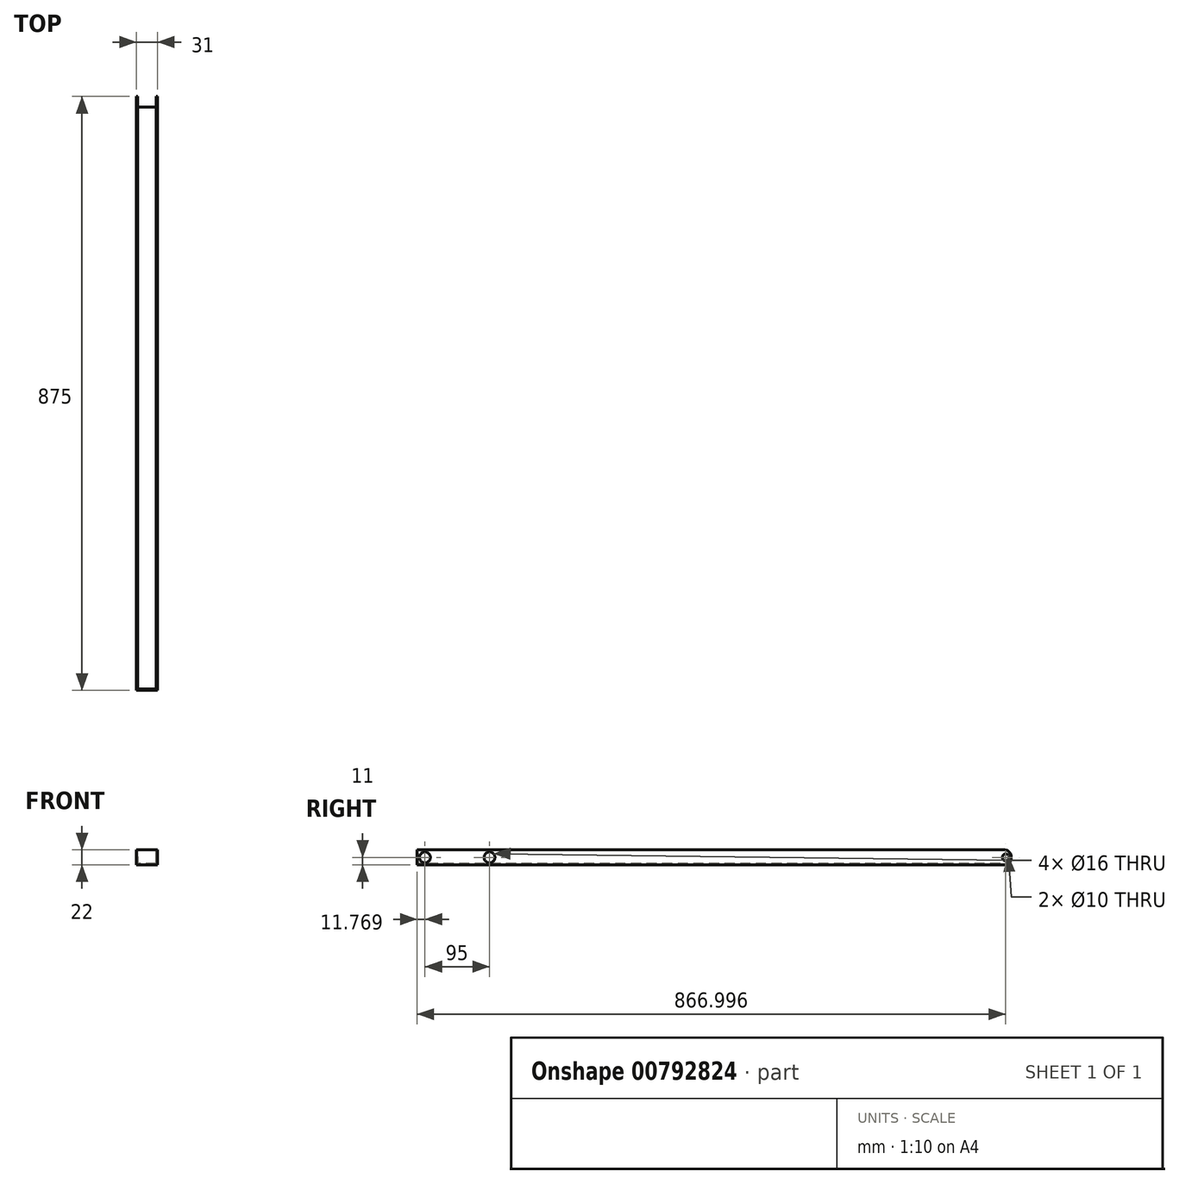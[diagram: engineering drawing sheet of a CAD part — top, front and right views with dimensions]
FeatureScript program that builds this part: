
annotation { "Feature Type Name" : "Feature", "Feature Type Description" : "" }
export const myFeature = defineFeature(function(context is Context, id is Id, definition is map)
    precondition{}
    {
        {
            var Q0;
            Q0=qCreatedBy(makeId("Right.planeOp"),FACE);
            var sketch = newSketch(context, id + "F0", { "sketchPlane" : qUnion([Q0])});
            skLineSegment(sketch, "E0", {"start": v(-388.26, 0) * mm, "end": v(486.74, 0) * mm});
            skLineSegment(sketch, "E1", {"start": v(486.74, 0) * mm, "end": v(486.74, -22) * mm});
            skLineSegment(sketch, "E2", {"start": v(486.74, -22) * mm, "end": v(-388.26, -22) * mm});
            skLineSegment(sketch, "E3", {"start": v(-388.26, -22) * mm, "end": v(-388.26, 0) * mm});
            skSolve(sketch);
        }
        {
            var Q0;
            Q0 = qSketchRegion(id + "F0", true);
            extrude(context, id + "F1", {"entities" : qUnion([Q0]), "oppositeDirection" : true, "depth" : 31 * mm, "offsetDistance" : 25 * mm});
        }
        {
            var Q0;
            Q0=makeQuery(id+"FNcDkWdHLqWzwqB_1.boolean.opBoolean","MERGE",FACE,{"derivedFrom":[makeQuery(id+"F1.opExtrude","SWEPT_FACE",FACE,{"disambiguationData":[OSD([sQuery(id+"F0.wireOp",EDGE,"E0")])]})],"fromTools":[makeQuery(id+"FNcDkWdHLqWzwqB_1.opExtrude","SWEPT_FACE",FACE,{"disambiguationData":[OSD([sQuery(id+"FCv60qlW79Pk3i8_1.wireOp",EDGE,"PrjJIeI4-ssgj-zgrI-7YpJ-pXO2Z5tQKrwP")])]})]});
            shell(context, id + "F2", {"entities" : qUnion([Q0]), "thickness" : 2 * mm});
        }
        {
            var Q0;
            Q0=makeQuery(id+"FVv2z1C1KTUzVl1_1.boolean.opBoolean","MERGE",FACE,{"derivedFrom":[makeQuery(id+"Fk6BJtRvKEo7X09_1.boolean.opBoolean","MERGE",FACE,{"derivedFrom":[makeQuery(id+"FNRSXFX3qVIVStC_1.boolean.opBoolean","MERGE",FACE,{"derivedFrom":[makeQuery(id+"F1.opExtrude","CAP_FACE",FACE,{"disambiguationData":[OSD([sQuery(id+"F0.wireOp",EDGE,"E0"),sQuery(id+"F0.wireOp",EDGE,"E1"),sQuery(id+"F0.wireOp",EDGE,"E2"),sQuery(id+"F0.wireOp",EDGE,"E3")])],"isStart":true}),makeQuery(id+"FNRSXFX3qVIVStC_1.opExtrude","CAP_FACE",FACE,{"disambiguationData":[OSD([sQuery(id+"FfsytLRgZImSpx3_1.wireOp",EDGE,"guVfW4hg-HYbG-UQzY-qkXY-AgcHQorrtYFj"),sQuery(id+"FfsytLRgZImSpx3_1.wireOp",EDGE,"ZCWRIXnY-XKVi-ryX6-uVYM-eQVDyBlf6B18"),sQuery(id+"FfsytLRgZImSpx3_1.wireOp",EDGE,"6apUsIMl-hWBS-8y3H-jMW6-ltsoOyLJVNbS"),sQuery(id+"FfsytLRgZImSpx3_1.wireOp",EDGE,"gpbRxTAZ-53LZ-ltw9-oope-mzS1HqgQM46F")])],"isStart":true})]}),makeQuery(id+"Fk6BJtRvKEo7X09_1.opExtrude","CAP_FACE",FACE,{"disambiguationData":[OSD([sQuery(id+"FWP3wo2K1PFairP_1.wireOp",EDGE,"RLKPXvGZ-6aeY-MFqp-uEFB-Y11XugVjV6vi"),sQuery(id+"FWP3wo2K1PFairP_1.wireOp",EDGE,"VqrrFjfu-vJZB-tzm9-Pqj7-21AsSRerqMTq"),sQuery(id+"FWP3wo2K1PFairP_1.wireOp",EDGE,"DV30RlPB-yelA-3BQe-yuDF-ZBDe1DssQMZR"),sQuery(id+"FWP3wo2K1PFairP_1.wireOp",EDGE,"hxL0ufJe-5V7Y-YkYO-v3yC-vdh2zJHQ3dM3")])],"isStart":true}),makeQuery(id+"Fk6BJtRvKEo7X09_1.opExtrude","CAP_FACE",FACE,{"disambiguationData":[OSD([sQuery(id+"FWP3wo2K1PFairP_1.wireOp",EDGE,"Iu78I8UH-Ag6m-vXnt-yIfC-VsHkMFwcecgq"),sQuery(id+"FWP3wo2K1PFairP_1.wireOp",EDGE,"J01mLQBO-0brp-1190-Uz3d-mbk1WVKgwclC"),sQuery(id+"FWP3wo2K1PFairP_1.wireOp",EDGE,"DArKGSrG-gMns-weNL-KKOz-bLA2HFYaYrMG"),sQuery(id+"FWP3wo2K1PFairP_1.wireOp",EDGE,"wbFtDD6o-eEzf-rPkh-OMWt-3cl9sizvQHqt")])],"isStart":true})]}),makeQuery(id+"FVv2z1C1KTUzVl1_1.opExtrude","CAP_FACE",FACE,{"disambiguationData":[OSD([sQuery(id+"FNLiDQGDlaEW116_1.wireOp",EDGE,"FMQFbGrz-yUS7-YStC-X8hH-naCITp3HSpcB"),sQuery(id+"FNLiDQGDlaEW116_1.wireOp",EDGE,"1a20oQKK-PTd7-pF8n-adkK-x5VS4rqthSRl"),sQuery(id+"FNLiDQGDlaEW116_1.wireOp",EDGE,"lPfx92Xd-sMOD-QXDu-w2bj-9ym4LUR5MAjY"),sQuery(id+"FNLiDQGDlaEW116_1.wireOp",EDGE,"eTXjAAXH-MWSY-cq12-PB3M-X8OxoKmDEWyC")])],"isStart":true}),makeQuery(id+"FVv2z1C1KTUzVl1_1.opExtrude","CAP_FACE",FACE,{"disambiguationData":[OSD([sQuery(id+"FNLiDQGDlaEW116_1.wireOp",EDGE,"V9W5izrU-Q6Zo-HlYU-XUtX-LOkD6KGmEAuB"),sQuery(id+"FNLiDQGDlaEW116_1.wireOp",EDGE,"562pbG6D-TJI1-XGno-75is-4YSaHXAUytCh"),sQuery(id+"FNLiDQGDlaEW116_1.wireOp",EDGE,"Zdfx7gO0-Y7jM-oHTw-9pvJ-OO3yxUAsWjtI"),sQuery(id+"FNLiDQGDlaEW116_1.wireOp",EDGE,"jmWXe39T-hYD2-V8mF-EcTK-DER7JQwctyas")])],"isStart":true}),makeQuery(id+"FVv2z1C1KTUzVl1_1.opExtrude","CAP_FACE",FACE,{"disambiguationData":[OSD([sQuery(id+"FNLiDQGDlaEW116_1.wireOp",EDGE,"KDKhPe1G-76aM-vKvb-EfsU-BXRDVSjyG5kg"),sQuery(id+"FNLiDQGDlaEW116_1.wireOp",EDGE,"2lfoMrka-jovZ-Rabm-Q0hQ-cbGMkZFnikdY"),sQuery(id+"FNLiDQGDlaEW116_1.wireOp",EDGE,"u8MqUk8a-5dgu-EIkQ-NQxV-EvjM6ESLjCmz"),sQuery(id+"FNLiDQGDlaEW116_1.wireOp",EDGE,"Ddv1R5dZ-CSrU-PeJ0-kcI9-YiED82pPoSU3")])],"isStart":true})]});
            var sketch = newSketch(context, id + "F3", { "sketchPlane" : qUnion([Q0])});
            skLineSegment(sketch, "E4", {"start": v(486.74, -11) * mm, "end": v(447.34, -11) * mm, "construction": true});
            skLineSegment(sketch, "E5", {"start": v(486.74, 12.78) * mm, "end": v(486.74, -40) * mm, "construction": true});
            skCircle(sketch, "E6", {"center": v(478.74, -11) * mm, "radius": 5 * mm});
            skSolve(sketch);
        }
        {
            var Q0;
            Q0 = qSketchRegion(id + "F3", true);
            extrude(context, id + "F4", {"entities" : qUnion([Q0]), "operationType" : NewBodyOperationType.REMOVE, "oppositeDirection" : true, "depth" : 61 * mm, "offsetDistance" : 25 * mm});
        }
        {
            var Q0;
            {var subQ7=sQuery(id+"F0.wireOp",EDGE,"E1");var subQ8=sQuery(id+"F0.wireOp",EDGE,"E0");var subQ14=makeQuery(id+"F1.opExtrude","SWEPT_FACE",FACE,{"disambiguationData":[OSD([subQ7])]});Q0=makeQuery(id+"Fk6BJtRvKEo7X09_1.boolean.opBoolean","SPLIT",FACE,{"disambiguationData":[TD([subQ14])],"derivedFrom":makeQuery(id+"FNRSXFX3qVIVStC_1.boolean.opBoolean","SPLIT",FACE,{"disambiguationData":[TD([subQ14])],"derivedFrom":makeQuery(id+"F1.opExtrude","SWEPT_FACE",FACE,{"disambiguationData":[OSD([subQ8])]})})});}
            var sketch = newSketch(context, id + "F5", { "sketchPlane" : qUnion([Q0])});
            skLineSegment(sketch, "E7.bottom", {"start": v(-10, 486.74) * mm, "end": v(-26, 486.74) * mm});
            skLineSegment(sketch, "E7.top", {"start": v(-10, 470.74) * mm, "end": v(-26, 470.74) * mm});
            skLineSegment(sketch, "E7.left", {"start": v(-10, 486.74) * mm, "end": v(-10, 470.74) * mm});
            skLineSegment(sketch, "E7.right", {"start": v(-26, 486.74) * mm, "end": v(-26, 470.74) * mm});
            skSolve(sketch);
        }
        {
            var Q0;
            Q0 = qSketchRegion(id + "F5", true);
            extrude(context, id + "F6", {"entities" : qUnion([Q0]), "operationType" : NewBodyOperationType.REMOVE, "oppositeDirection" : true, "depth" : 46 * mm, "offsetDistance" : 25 * mm});
        }
        {
            var Q0;
            Q0=makeQuery(id+"FVv2z1C1KTUzVl1_1.boolean.opBoolean","MERGE",FACE,{"derivedFrom":[makeQuery(id+"Fk6BJtRvKEo7X09_1.boolean.opBoolean","MERGE",FACE,{"derivedFrom":[makeQuery(id+"FNRSXFX3qVIVStC_1.boolean.opBoolean","MERGE",FACE,{"derivedFrom":[makeQuery(id+"F1.opExtrude","CAP_FACE",FACE,{"disambiguationData":[OSD([sQuery(id+"F0.wireOp",EDGE,"E0"),sQuery(id+"F0.wireOp",EDGE,"E1"),sQuery(id+"F0.wireOp",EDGE,"E2"),sQuery(id+"F0.wireOp",EDGE,"E3")])],"isStart":true}),makeQuery(id+"FNRSXFX3qVIVStC_1.opExtrude","CAP_FACE",FACE,{"disambiguationData":[OSD([sQuery(id+"FfsytLRgZImSpx3_1.wireOp",EDGE,"guVfW4hg-HYbG-UQzY-qkXY-AgcHQorrtYFj"),sQuery(id+"FfsytLRgZImSpx3_1.wireOp",EDGE,"ZCWRIXnY-XKVi-ryX6-uVYM-eQVDyBlf6B18"),sQuery(id+"FfsytLRgZImSpx3_1.wireOp",EDGE,"6apUsIMl-hWBS-8y3H-jMW6-ltsoOyLJVNbS"),sQuery(id+"FfsytLRgZImSpx3_1.wireOp",EDGE,"gpbRxTAZ-53LZ-ltw9-oope-mzS1HqgQM46F")])],"isStart":true})]}),makeQuery(id+"Fk6BJtRvKEo7X09_1.opExtrude","CAP_FACE",FACE,{"disambiguationData":[OSD([sQuery(id+"FWP3wo2K1PFairP_1.wireOp",EDGE,"RLKPXvGZ-6aeY-MFqp-uEFB-Y11XugVjV6vi"),sQuery(id+"FWP3wo2K1PFairP_1.wireOp",EDGE,"VqrrFjfu-vJZB-tzm9-Pqj7-21AsSRerqMTq"),sQuery(id+"FWP3wo2K1PFairP_1.wireOp",EDGE,"DV30RlPB-yelA-3BQe-yuDF-ZBDe1DssQMZR"),sQuery(id+"FWP3wo2K1PFairP_1.wireOp",EDGE,"hxL0ufJe-5V7Y-YkYO-v3yC-vdh2zJHQ3dM3")])],"isStart":true}),makeQuery(id+"Fk6BJtRvKEo7X09_1.opExtrude","CAP_FACE",FACE,{"disambiguationData":[OSD([sQuery(id+"FWP3wo2K1PFairP_1.wireOp",EDGE,"Iu78I8UH-Ag6m-vXnt-yIfC-VsHkMFwcecgq"),sQuery(id+"FWP3wo2K1PFairP_1.wireOp",EDGE,"J01mLQBO-0brp-1190-Uz3d-mbk1WVKgwclC"),sQuery(id+"FWP3wo2K1PFairP_1.wireOp",EDGE,"DArKGSrG-gMns-weNL-KKOz-bLA2HFYaYrMG"),sQuery(id+"FWP3wo2K1PFairP_1.wireOp",EDGE,"wbFtDD6o-eEzf-rPkh-OMWt-3cl9sizvQHqt")])],"isStart":true})]}),makeQuery(id+"FVv2z1C1KTUzVl1_1.opExtrude","CAP_FACE",FACE,{"disambiguationData":[OSD([sQuery(id+"FNLiDQGDlaEW116_1.wireOp",EDGE,"FMQFbGrz-yUS7-YStC-X8hH-naCITp3HSpcB"),sQuery(id+"FNLiDQGDlaEW116_1.wireOp",EDGE,"1a20oQKK-PTd7-pF8n-adkK-x5VS4rqthSRl"),sQuery(id+"FNLiDQGDlaEW116_1.wireOp",EDGE,"lPfx92Xd-sMOD-QXDu-w2bj-9ym4LUR5MAjY"),sQuery(id+"FNLiDQGDlaEW116_1.wireOp",EDGE,"eTXjAAXH-MWSY-cq12-PB3M-X8OxoKmDEWyC")])],"isStart":true}),makeQuery(id+"FVv2z1C1KTUzVl1_1.opExtrude","CAP_FACE",FACE,{"disambiguationData":[OSD([sQuery(id+"FNLiDQGDlaEW116_1.wireOp",EDGE,"V9W5izrU-Q6Zo-HlYU-XUtX-LOkD6KGmEAuB"),sQuery(id+"FNLiDQGDlaEW116_1.wireOp",EDGE,"562pbG6D-TJI1-XGno-75is-4YSaHXAUytCh"),sQuery(id+"FNLiDQGDlaEW116_1.wireOp",EDGE,"Zdfx7gO0-Y7jM-oHTw-9pvJ-OO3yxUAsWjtI"),sQuery(id+"FNLiDQGDlaEW116_1.wireOp",EDGE,"jmWXe39T-hYD2-V8mF-EcTK-DER7JQwctyas")])],"isStart":true}),makeQuery(id+"FVv2z1C1KTUzVl1_1.opExtrude","CAP_FACE",FACE,{"disambiguationData":[OSD([sQuery(id+"FNLiDQGDlaEW116_1.wireOp",EDGE,"KDKhPe1G-76aM-vKvb-EfsU-BXRDVSjyG5kg"),sQuery(id+"FNLiDQGDlaEW116_1.wireOp",EDGE,"2lfoMrka-jovZ-Rabm-Q0hQ-cbGMkZFnikdY"),sQuery(id+"FNLiDQGDlaEW116_1.wireOp",EDGE,"u8MqUk8a-5dgu-EIkQ-NQxV-EvjM6ESLjCmz"),sQuery(id+"FNLiDQGDlaEW116_1.wireOp",EDGE,"Ddv1R5dZ-CSrU-PeJ0-kcI9-YiED82pPoSU3")])],"isStart":true})]});
            var sketch = newSketch(context, id + "F7", { "sketchPlane" : qUnion([Q0])});
            skLineSegment(sketch, "E8", {"start": v(-402.66, -11) * mm, "end": v(-242.66, -11) * mm, "construction": true});
            skPoint(sketch, "E8.startSnap0", {"position": v(-388.26, -11) * mm});
            skCircle(sketch, "E9", {"center": v(-376.5, -11) * mm, "radius": 8 * mm});
            skCircle(sketch, "E10", {"center": v(-281.5, -11) * mm, "radius": 8 * mm});
            skSolve(sketch);
        }
        {
            var Q0;
            Q0 = qSketchRegion(id + "F7", true);
            extrude(context, id + "F8", {"entities" : qUnion([Q0]), "operationType" : NewBodyOperationType.REMOVE, "oppositeDirection" : true, "depth" : 96 * mm, "offsetDistance" : 25 * mm});
        }
        {
            var Q0;
            {var subQ0=sQuery(id+"F0.wireOp",EDGE,"E0");var subQ1=sQuery(id+"F0.wireOp",EDGE,"E1");Q0=makeQuery(id+"F6.boolean.opBoolean","SPLIT",EDGE,{"disambiguationData":[TD([makeQuery(id+"F6.opExtrude","SWEPT_FACE",FACE,{"disambiguationData":[OSD([sQuery(id+"F5.wireOp",EDGE,"E7.left")])]})])],"derivedFrom":makeQuery(id+"F1.opExtrude","SWEPT_EDGE",EDGE,{"disambiguationData":[OSD([subQ0,subQ1])]})});}
            var Q1;
            {var subQ0=sQuery(id+"F0.wireOp",EDGE,"E0");var subQ1=sQuery(id+"F0.wireOp",EDGE,"E1");Q1=makeQuery(id+"F6.boolean.opBoolean","SPLIT",EDGE,{"disambiguationData":[TD([makeQuery(id+"F6.opExtrude","SWEPT_FACE",FACE,{"disambiguationData":[OSD([sQuery(id+"F5.wireOp",EDGE,"E7.right")])]})])],"derivedFrom":makeQuery(id+"F1.opExtrude","SWEPT_EDGE",EDGE,{"disambiguationData":[OSD([subQ0,subQ1])]})});}
            var Q2;
            {var subQ1=sQuery(id+"F0.wireOp",EDGE,"E2");var subQ2=sQuery(id+"F0.wireOp",EDGE,"E1");Q2=makeQuery(id+"F6.boolean.opBoolean","SPLIT",EDGE,{"disambiguationData":[TD([makeQuery(id+"F6.opExtrude","SWEPT_FACE",FACE,{"disambiguationData":[OSD([sQuery(id+"F5.wireOp",EDGE,"E7.left")])]})])],"derivedFrom":makeQuery(id+"F2.opShell","OFFSET_EDGE",EDGE,{"disambiguationData":[OSD([subQ2,subQ1])]})});}
            var Q3;
            {var subQ0=sQuery(id+"F0.wireOp",EDGE,"E2");var subQ1=sQuery(id+"F0.wireOp",EDGE,"E1");Q3=makeQuery(id+"F6.boolean.opBoolean","SPLIT",EDGE,{"disambiguationData":[TD([makeQuery(id+"F6.opExtrude","SWEPT_FACE",FACE,{"disambiguationData":[OSD([sQuery(id+"F5.wireOp",EDGE,"E7.left")])]})])],"derivedFrom":makeQuery(id+"F1.opExtrude","SWEPT_EDGE",EDGE,{"disambiguationData":[OSD([subQ1,subQ0])]})});}
            var Q4;
            {var subQ1=sQuery(id+"F0.wireOp",EDGE,"E2");var subQ2=sQuery(id+"F0.wireOp",EDGE,"E1");Q4=makeQuery(id+"F6.boolean.opBoolean","SPLIT",EDGE,{"disambiguationData":[TD([makeQuery(id+"F6.opExtrude","SWEPT_FACE",FACE,{"disambiguationData":[OSD([sQuery(id+"F5.wireOp",EDGE,"E7.right")])]})])],"derivedFrom":makeQuery(id+"F2.opShell","OFFSET_EDGE",EDGE,{"disambiguationData":[OSD([subQ2,subQ1])]})});}
            var Q5;
            {var subQ0=sQuery(id+"F0.wireOp",EDGE,"E2");var subQ1=sQuery(id+"F0.wireOp",EDGE,"E1");Q5=makeQuery(id+"F6.boolean.opBoolean","SPLIT",EDGE,{"disambiguationData":[TD([makeQuery(id+"F6.opExtrude","SWEPT_FACE",FACE,{"disambiguationData":[OSD([sQuery(id+"F5.wireOp",EDGE,"E7.right")])]})])],"derivedFrom":makeQuery(id+"F1.opExtrude","SWEPT_EDGE",EDGE,{"disambiguationData":[OSD([subQ1,subQ0])]})});}
            fillet(context, id + "F9", {"entities" : qUnion([Q0, Q1, Q2, Q3, Q4, Q5]), "tangentPropagation" : true, "radius" : 10 * mm, "defaultsChanged" : false, "vertexSettings" : [], "allowEdgeOverflow" : false});
        }
        {
            var Q0;
            Q0=makeQuery(id+"F2.opShell","OFFSET_FACE",FACE,{"disambiguationData":[OSD([sQuery(id+"F0.wireOp",EDGE,"E2")])]});
            var sketch = newSketch(context, id + "F10", { "sketchPlane" : qUnion([Q0])});
            skLineSegment(sketch, "E11", {"start": v(-29, 470.74) * mm, "end": v(-29, 492.25) * mm});
            skLineSegment(sketch, "E12", {"start": v(-29, 492.25) * mm, "end": v(-2, 492.25) * mm});
            skLineSegment(sketch, "E13", {"start": v(-2, 492.25) * mm, "end": v(-2, 470.74) * mm});
            skLineSegment(sketch, "E14", {"start": v(-2, 470.74) * mm, "end": v(-29, 470.74) * mm});
            skSolve(sketch);
        }
        {
            var Q0;
            Q0 = qSketchRegion(id + "F10", true);
            extrude(context, id + "F11", {"entities" : qUnion([Q0]), "operationType" : NewBodyOperationType.REMOVE, "oppositeDirection" : true, "depth" : 25 * mm, "offsetDistance" : 25 * mm});
        }
        {
            var Q0;
            Q0=makeQuery(id+"F2.opShell","OFFSET_FACE",FACE,{"disambiguationData":[OSD([sQuery(id+"F0.wireOp",EDGE,"E2")])]});
            var sketch = newSketch(context, id + "F12", { "sketchPlane" : qUnion([Q0])});
            skLineSegment(sketch, "E15", {"start": v(-2, 491.58) * mm, "end": v(-2, 473.22) * mm});
            skLineSegment(sketch, "E16", {"start": v(-2, 473.22) * mm, "end": v(-29, 473.22) * mm});
            skLineSegment(sketch, "E17", {"start": v(-29, 473.22) * mm, "end": v(-29, 491.58) * mm});
            skLineSegment(sketch, "E18", {"start": v(-29, 491.58) * mm, "end": v(-2, 491.58) * mm});
            skSolve(sketch);
        }
        {
            var Q0;
            Q0 = qSketchRegion(id + "F12", true);
            extrude(context, id + "F13", {"entities" : qUnion([Q0]), "operationType" : NewBodyOperationType.REMOVE, "depth" : 25 * mm, "offsetDistance" : 25 * mm});
        }
    });
